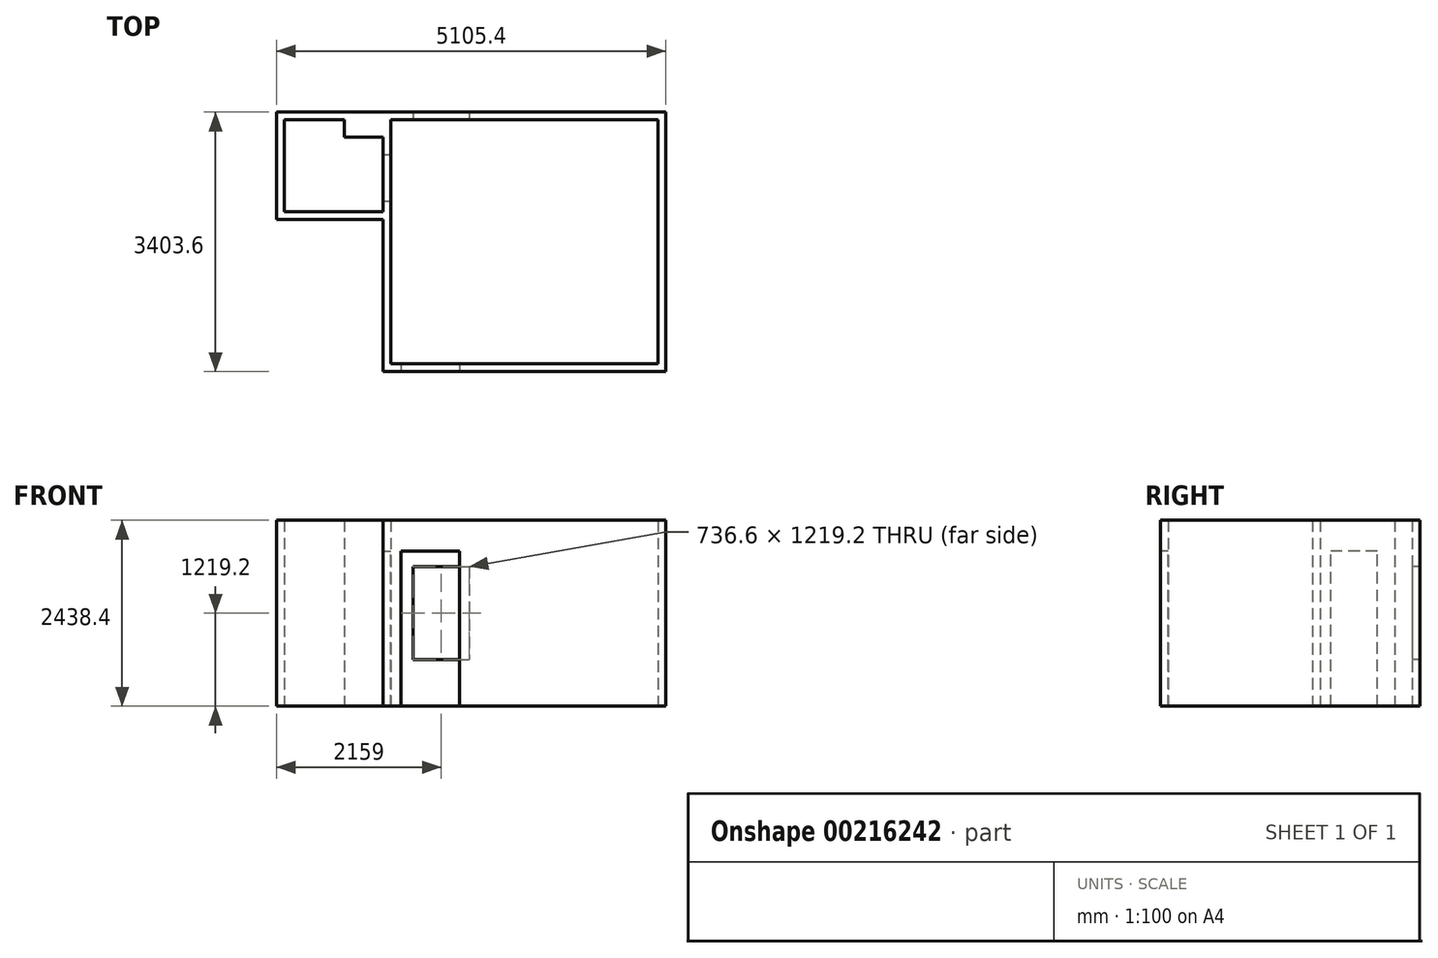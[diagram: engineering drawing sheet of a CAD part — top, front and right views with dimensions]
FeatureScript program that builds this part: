
annotation { "Feature Type Name" : "Feature", "Feature Type Description" : "" }
export const myFeature = defineFeature(function(context is Context, id is Id, definition is map)
    precondition{}
    {
        {
            var Q0;
            Q0=qCreatedBy(makeId("Top.planeOp"),FACE);
            var sketch = newSketch(context, id + "F0", { "sketchPlane" : qUnion([Q0])});
            skLineSegment(sketch, "E0", {"start": v(0, 0) * mm, "end": v(0, 3200.4) * mm});
            skLineSegment(sketch, "E1", {"start": v(0, 3200.4) * mm, "end": v(-3505.2, 3200.4) * mm});
            skLineSegment(sketch, "E2", {"start": v(-4902.2, 3200.4) * mm, "end": v(-4902.2, 1993.9) * mm});
            skLineSegment(sketch, "E3", {"start": v(-4902.2, 1993.9) * mm, "end": v(-3606.8, 1993.9) * mm});
            skLineSegment(sketch, "E4", {"start": v(-3505.2, 3200.4) * mm, "end": v(-3505.2, 0) * mm});
            skLineSegment(sketch, "E5", {"start": v(-3505.2, 0) * mm, "end": v(0, 0) * mm});
            skLineSegment(sketch, "E6.0", {"start": v(101.6, -101.6) * mm, "end": v(101.6, 3302) * mm});
            skLineSegment(sketch, "E6.1", {"start": v(-5003.8, 3302) * mm, "end": v(-5003.8, 1892.3) * mm});
            skLineSegment(sketch, "E6.2", {"start": v(-5003.8, 1892.3) * mm, "end": v(-3606.8, 1892.3) * mm});
            skLineSegment(sketch, "E6.3", {"start": v(101.6, 3302) * mm, "end": v(-5003.8, 3302) * mm});
            skLineSegment(sketch, "E6.4", {"start": v(-3606.8, 2971.8) * mm, "end": v(-3606.8, 1993.9) * mm});
            skLineSegment(sketch, "E6.5", {"start": v(-3606.8, -101.6) * mm, "end": v(101.6, -101.6) * mm});
            skLineSegment(sketch, "E7", {"start": v(-4114.8, 3200.4) * mm, "end": v(-4114.8, 2971.8) * mm});
            skLineSegment(sketch, "E8", {"start": v(-4114.8, 2971.8) * mm, "end": v(-3606.8, 2971.8) * mm});
            skLineSegment(sketch, "E9.trimOffspring", {"start": v(-4114.8, 3200.4) * mm, "end": v(-4902.2, 3200.4) * mm});
            skLineSegment(sketch, "E10.trimOffspring", {"start": v(-3606.8, 1892.3) * mm, "end": v(-3606.8, -101.6) * mm});
            skSolve(sketch);
        }
        {
            var Q0;
            Q0=makeQuery(id+"F0.imprint","IMPRINT",FACE,{"disambiguationData":[TD([[makeQuery(id+"F0.imprint","IMPRINT",EDGE,{"derivedFrom":sQuery(id+"F0.wireOp",EDGE,"E0")}),-1.0]])]});
            extrude(context, id + "F1", {"entities" : qUnion([Q0]), "depth" : 2438.4 * mm});
        }
        {
            var Q0;
            Q0=makeQuery(id+"F1.opExtrude","SWEPT_FACE",FACE,{"disambiguationData":[OSD([sQuery(id+"F0.wireOp",EDGE,"E6.5")])]});
            var sketch = newSketch(context, id + "F2", { "sketchPlane" : qUnion([Q0])});
            skLineSegment(sketch, "E11.bottom", {"start": v(-3371.85, 0) * mm, "end": v(-2603.5, 0) * mm});
            skLineSegment(sketch, "E11.top", {"start": v(-3371.85, 2032) * mm, "end": v(-2603.5, 2032) * mm});
            skLineSegment(sketch, "E11.left", {"start": v(-3371.85, 0) * mm, "end": v(-3371.85, 2032) * mm});
            skLineSegment(sketch, "E11.right", {"start": v(-2603.5, 0) * mm, "end": v(-2603.5, 2032) * mm});
            skSolve(sketch);
        }
        {
            var Q0;
            Q0=makeQuery(id+"F2.imprint","IMPRINT",FACE,{"disambiguationData":[TD([[makeQuery(id+"F2.imprint","IMPRINT",EDGE,{"derivedFrom":sQuery(id+"F2.wireOp",EDGE,"E11.bottom")}),1.0]])]});
            extrude(context, id + "F3", {"entities" : qUnion([Q0]), "operationType" : NewBodyOperationType.REMOVE, "oppositeDirection" : true, "depth" : 101.6 * mm});
        }
        {
            var Q0;
            Q0=makeQuery(id+"F1.opExtrude","SWEPT_FACE",FACE,{"disambiguationData":[OSD([sQuery(id+"F0.wireOp",EDGE,"E1")])]});
            var sketch = newSketch(context, id + "F4", { "sketchPlane" : qUnion([Q0])});
            skLineSegment(sketch, "E12.bottom", {"start": v(-3213.1, 1828.8) * mm, "end": v(-2476.5, 1828.8) * mm});
            skLineSegment(sketch, "E12.top", {"start": v(-3213.1, 609.6) * mm, "end": v(-2476.5, 609.6) * mm});
            skLineSegment(sketch, "E12.left", {"start": v(-3213.1, 1828.8) * mm, "end": v(-3213.1, 609.6) * mm});
            skLineSegment(sketch, "E12.right", {"start": v(-2476.5, 1828.8) * mm, "end": v(-2476.5, 609.6) * mm});
            skSolve(sketch);
        }
        {
            var Q0;
            Q0=makeQuery(id+"F4.imprint","IMPRINT",FACE,{"disambiguationData":[TD([[makeQuery(id+"F4.imprint","IMPRINT",EDGE,{"derivedFrom":sQuery(id+"F4.wireOp",EDGE,"E12.bottom")}),-1.0]])]});
            extrude(context, id + "F5", {"entities" : qUnion([Q0]), "operationType" : NewBodyOperationType.REMOVE, "oppositeDirection" : true, "depth" : 101.6 * mm});
        }
        {
            var Q0;
            Q0=makeQuery(id+"F1.opExtrude","SWEPT_FACE",FACE,{"disambiguationData":[OSD([sQuery(id+"F0.wireOp",EDGE,"E4")])]});
            var sketch = newSketch(context, id + "F6", { "sketchPlane" : qUnion([Q0])});
            skLineSegment(sketch, "E13.bottom", {"start": v(2743.2, 0) * mm, "end": v(2133.6, 0) * mm});
            skLineSegment(sketch, "E13.top", {"start": v(2743.2, 2032) * mm, "end": v(2133.6, 2032) * mm});
            skLineSegment(sketch, "E13.left", {"start": v(2743.2, 0) * mm, "end": v(2743.2, 2032) * mm});
            skLineSegment(sketch, "E13.right", {"start": v(2133.6, 0) * mm, "end": v(2133.6, 2032) * mm});
            skSolve(sketch);
        }
        {
            var Q0;
            Q0=makeQuery(id+"F6.imprint","IMPRINT",FACE,{"disambiguationData":[TD([[makeQuery(id+"F6.imprint","IMPRINT",EDGE,{"derivedFrom":sQuery(id+"F6.wireOp",EDGE,"E13.bottom")}),-1.0]])]});
            extrude(context, id + "F7", {"entities" : qUnion([Q0]), "operationType" : NewBodyOperationType.REMOVE, "oppositeDirection" : true, "depth" : 101.6 * mm});
        }
    });
